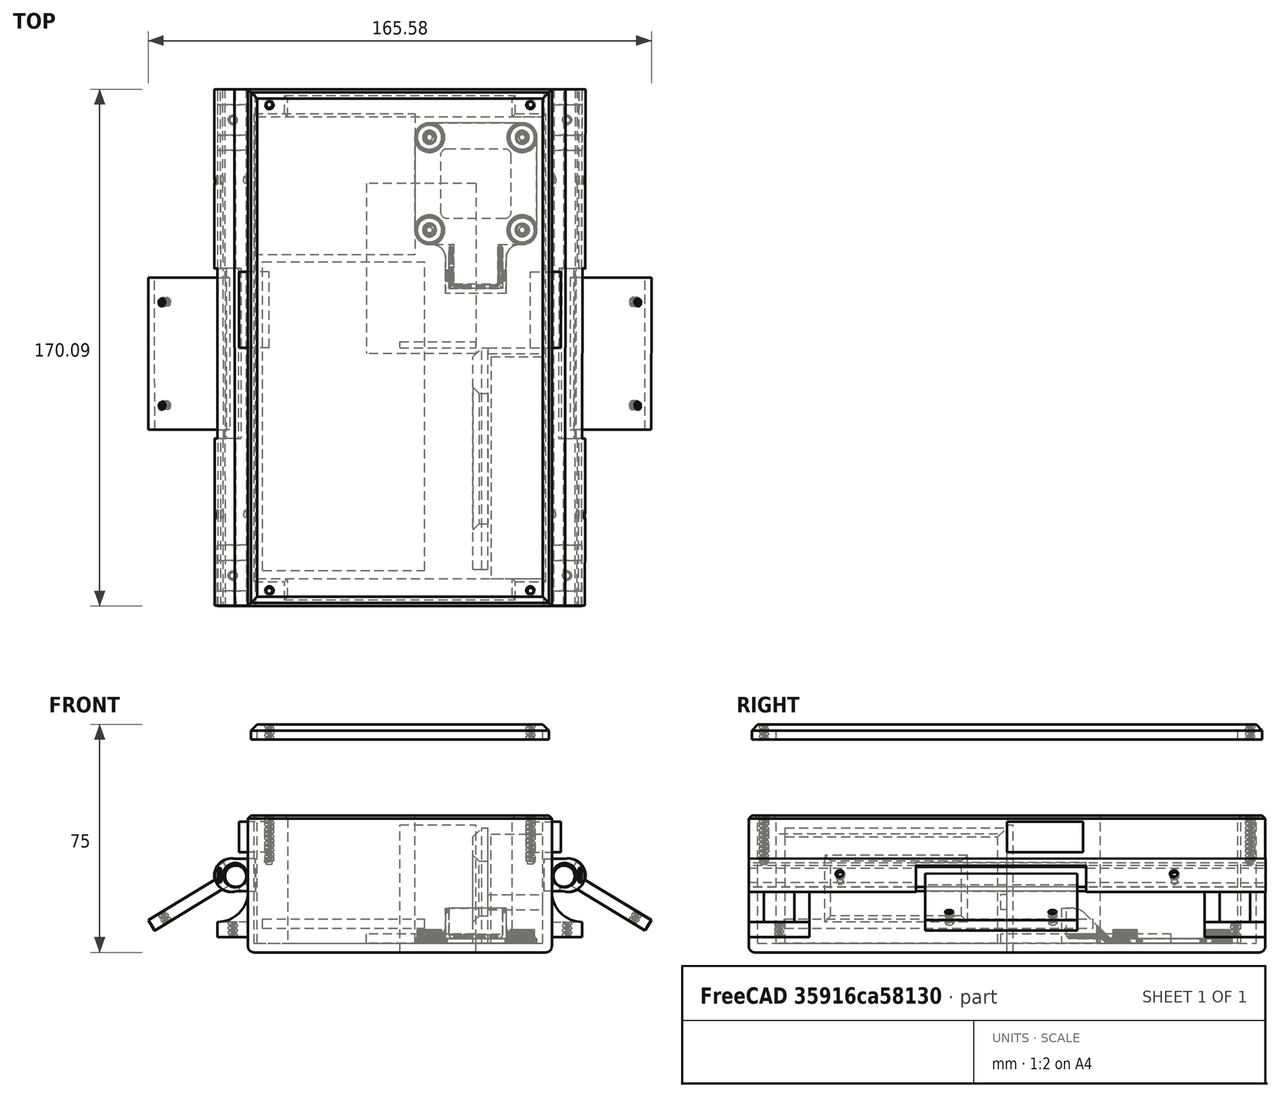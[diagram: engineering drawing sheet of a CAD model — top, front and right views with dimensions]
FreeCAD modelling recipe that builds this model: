
FCSTD DOCUMENT  (FreeCAD 0.21R33694 (Git))
Label: boceto-carcasa-reducido
License: Creative Commons Attribution-NonCommercial-ShareAlike 4.0
LicenseURL: https://creativecommons.org/licenses/by-nc-sa/4.0/
objects: Part::Box×18, Part::Fuse×14, Part::Cut×13, Part::Mirroring×10, Part::Feature×9, Part::Chamfer×5, Sketcher::SketchObject×3, Part::Cylinder×3, Part::Extrusion×3, Part::Fillet×2, Mesh::Feature×1, Part::MultiFuse×1, Part::Compound×1, App::LinkGroup×1, PartDesign::FeatureBase×1, PartDesign::Body×1
note: 84 computed .brp shape members not serialized (recipe doc carries the construction recipe); baked Part::Feature solids carry a one-line shape summary decoded from their .brp

FEATURE [Sketcher::SketchObject] Sketch  label="case-taladros"
  FullyConstrained = true
  MapMode = 5
  Support = -> [XY_Plane]
  sketch-geometry (4):
    g0: LineSegment StartX=-50 StartY=85 StartZ=0 EndX=50 EndY=85 EndZ=0
    g1: LineSegment StartX=50 StartY=85 StartZ=0 EndX=50 EndY=-85 EndZ=0
    g2: LineSegment StartX=50 StartY=-85 StartZ=0 EndX=-50 EndY=-85 EndZ=0
    g3: LineSegment StartX=-50 StartY=-85 StartZ=0 EndX=-50 EndY=85 EndZ=0
  constraints (10):
    c: Coincident(g0,g1)
    c: Coincident(g1,g2)
    c: Coincident(g2,g3)
    c: Coincident(g3,g0)
    c: Horizontal(g2)
    c: Vertical(g1)
    c: Symmetric(g0,g0,g-2)
    c: Symmetric(g2,g0,g-1)
    c: DistanceY(g3,g3) = 170
    c: DistanceX(g0,g0) = 100
FEATURE [Part::Box] Box001  label="vaciado"
  AttacherType = Attacher::AttachEngine3D
  Height = 42
  Length = 94
  Placement = pos=(-47,-76,3) rot=(0,0,1;0rad)
  Width = 152
FEATURE [Mesh::Feature] Arduino_Bumper_0005  label="Arduino-uno-case"
  Placement = pos=(-19,-40,5) rot=(0,0,1;-1.5708rad)
FEATURE [Sketcher::SketchObject] Sketch008  label="tapa-taladros"
  FullyConstrained = true
  MapMode = 5
  sketch-geometry (4):
    g0: LineSegment StartX=-49 StartY=84 StartZ=0 EndX=49 EndY=84 EndZ=0
    g1: LineSegment StartX=49 StartY=84 StartZ=0 EndX=49 EndY=-84 EndZ=0
    g2: LineSegment StartX=49 StartY=-84 StartZ=0 EndX=-49 EndY=-84 EndZ=0
    g3: LineSegment StartX=-49 StartY=-84 StartZ=0 EndX=-49 EndY=84 EndZ=0
  constraints (10):
    c: Coincident(g0,g1)
    c: Coincident(g1,g2)
    c: Coincident(g2,g3)
    c: Coincident(g3,g0)
    c: Horizontal(g2)
    c: Vertical(g1)
    c: Symmetric(g0,g0,g-2)
    c: Symmetric(g2,g0,g-1)
    c: DistanceY(g3,g3) = 168
    c: DistanceX(g0,g0) = 98
FEATURE [Part::Box] Box010  label="restriccion-lipo"
  AttacherType = Attacher::AttachEngine3D
  Height = 38
  Length = 5
  Placement = pos=(17,-75,5) rot=(0,0,1;0rad)
  Width = 73
FEATURE [Part::Box] Box011  label="restriccion-lipo001"
  AttacherType = Attacher::AttachEngine3D
  Height = 18
  Length = 7
  Placement = pos=(16,-60,14) rot=(0,0,1;0rad)
  Width = 43
FEATURE [Part::Cut] Cut028
  Base = -> Box010
  Refine = true
  Tool = -> Box011
FEATURE [Part::Chamfer] Chamfer002
  Base = -> Cut028
  Edges = 2 edges r=3: [Edge2,Edge4]
FEATURE [Part::Chamfer] Chamfer003
  Base = -> Chamfer002
  Edges = 4 edges r=2: [Edge5,Edge6,Edge7,Edge8]
FEATURE [Part::Box] Box012  label="Cube004"
  AttacherType = Attacher::AttachEngine3D
  Height = 5
  Length = 20
  Placement = pos=(20,-4,16) rot=(0,0,1;0rad)
  Width = 2
FEATURE [Part::Fuse] Fusion001032  label="rejillas-lipo"
  Base = -> Chamfer003
  Placement = pos=(7,2,-2) rot=(0,0,1;0rad)
  Refine = true
  Tool = -> Box012
FEATURE [Part::Box] Box013  label="PDB-space"
  AttacherType = Attacher::AttachEngine3D
  Height = 3
  Length = 36
  Placement = pos=(25,54,3) rot=(0,0,1;3.14159rad)
  Width = 56
FEATURE [Part::Feature] Compound001  label="pcb-support"
  Placement = pos=(25,54,3) rot=(0,0,1;3.14159rad)
  shape: bbox 40 x 56.1 x 12 mm, 27565 faces, 3 solids (baked)
FEATURE [Part::Box] Box014  label="free-space"
  AttacherType = Attacher::AttachEngine3D
  Height = 42
  Length = 46.3
  Placement = pos=(-48,77,3) rot=(0,0,-1;1.5708rad)
  Width = 53
FEATURE [Part::Box] Box015  label="Cubo002"
  AttacherType = Attacher::AttachEngine3D
  Height = 4
  Length = 50
  Placement = pos=(-25,22,-7.5) rot=(0,0,1;0rad)
  Width = 30
FEATURE [Part::Box] Box016  label="cubo-corte"
  AttacherType = Attacher::AttachEngine3D
  Height = 20
  Length = 56
  Placement = pos=(-145,75,-20) rot=(0,0,1;0rad)
  Width = 16
FEATURE [Part::Cylinder] Cylinder007  label="Cilindro-movil"
  Angle = 360
  AttacherType = Attacher::AttachEngine3D
  FirstAngle = 0
  Height = 170
  Placement = pos=(-200,92,-6) rot=(0,1,0;1.5708rad)
  Radius = 3.5
  SecondAngle = 0
FEATURE [Part::Feature] Fusion001034  label="Rosca macho012"
  Placement = pos=(-17,27,-10) rot=(0,0,1;0rad)
  shape: bbox 3.919 x 4.387 x 44 mm, 35 faces (baked)
FEATURE [Part::Feature] Fusion001035  label="Rosca macho013"
  Placement = pos=(17,27,-10) rot=(0,0,1;0rad)
  shape: bbox 3.919 x 4.387 x 44 mm, 35 faces (baked)
FEATURE [Part::MultiFuse] Fusion001036
  Refine = true
  Shapes = -> [Fusion001034,Fusion001035]
FEATURE [Part::Cut] Cut030  label="Soporte_eje001"
  Base = -> Box015
  Placement = pos=(-117,38,0) rot=(0,0,1;0rad)
  Refine = true
  Tool = -> Fusion001036
FEATURE [Part::Feature] Fusion001037  label="Rosca macho014"
  Placement = pos=(-170,93.75,-8.78) rot=(0.819304,0.219813,-0.52955;0.936369rad)
  shape: bbox 4.221 x 33 x 32.52 mm, 35 faces (baked)
FEATURE [Part::Feature] Fusion001038  label="Rosca macho015"
  Placement = pos=(-60,93.75,-8.78) rot=(0.819304,0.219813,-0.52955;0.936369rad)
  shape: bbox 4.221 x 33 x 32.52 mm, 35 faces (baked)
FEATURE [Part::Fuse] Fusion001033  label="roscas002"
  Base = -> Fusion001037
  Refine = true
  Tool = -> Fusion001038
FEATURE [Part::Fuse] Fusion001039  label="cilindro-movil001"
  Base = -> Cut030
  Refine = true
  Tool = -> Cylinder007
FEATURE [Sketcher::SketchObject] Sketch009
  FullyConstrained = false
  MapMode = 5
  Placement = pos=(0,0,0) rot=(0.57735,0.57735,0.57735;2.0944rad)
  Support = -> [YZ_Plane004]
  sketch-geometry (9):
    g0: ArcOfCircle CenterX=0 CenterY=0 CenterZ=0 NormalX=0 NormalY=0 NormalZ=1 AngleXU=0 Radius=5.5 StartAngle=6.08579 EndAngle=9.70025
    g1: Circle CenterX=0 CenterY=-1.19343 CenterZ=0 NormalX=0 NormalY=0 NormalZ=1 AngleXU=0 Radius=4
    g2: LineSegment StartX=-2.36 StartY=4.37566 StartZ=0 EndX=2.36 EndY=4.37566 EndZ=0
    g3: LineSegment StartX=2.36 StartY=4.37566 StartZ=0 EndX=2.36 EndY=3.44566 EndZ=0
    g4: LineSegment StartX=2.36 StartY=3.44566 StartZ=0 EndX=-2.36 EndY=3.44566 EndZ=0
    g5: LineSegment StartX=-2.36 StartY=3.44566 StartZ=0 EndX=-2.36 EndY=4.37566 EndZ=0
    g6: LineSegment StartX=-5.29263 StartY=-1.49602 StartZ=0 EndX=-5.29263 EndY=-8 EndZ=0
    g7: LineSegment StartX=-5.29263 StartY=-8 StartZ=0 EndX=5.39319 EndY=-8 EndZ=0
    g8: LineSegment StartX=5.39319 StartY=-8 StartZ=0 EndX=5.39319 EndY=-1.07864 EndZ=0
  constraints (21):
    c: Coincident(g0,g-1)
    c: Coincident(g2,g3)
    c: Coincident(g3,g4)
    c: Coincident(g4,g5)
    c: Coincident(g5,g2)
    c: Horizontal(g4)
    c: Vertical(g3)
    c: Vertical(g5)
    c: Symmetric(g2,g2,g-2)
    c: PointOnObject(g1,g-2)
    c: Radius(g0) = 5.5
    c: Radius(g1) = 4
    c: DistanceY(g5,g5) = 0.93
    c: DistanceX(g2,g2) = 4.72
    c: Coincident(g6,g7)
    c: Coincident(g7,g8)
    c: Horizontal(g7)
    c: Vertical(g6)
    c: Vertical(g8)
    c: Coincident(g0,g8)
    c: Coincident(g6,g0)
FEATURE [Part::Extrusion] Extrude003  label="cilindro-fijo001"
  Base = -> Sketch009
  Dir = (1,-1e-16,1e-16)
  DirMode = 2
  FaceMakerClass = Part::FaceMakerBullseye
  LengthFwd = 170
  LengthRev = 0
  Placement = pos=(-200,91,-5) rot=(1,0,0;1.02974rad)
  Solid = true
  Symmetric = false
FEATURE [Part::Cut] Cut029
  Base = -> Extrude003
  Refine = true
  Tool = -> Fusion001033
FEATURE [Part::Cut] Cut031  label="fijacion-brazo"
  Base = -> Cut029
  Refine = true
  Tool = -> Box016
FEATURE [Part::Compound] Compound  label="brazo-mejorados"
  Links = -> [Cut031,Fusion001039]
  Placement = pos=(136,115,-16.54) rot=(0.259987,0.259987,0.929954;1.64236rad)
FEATURE [Part::Mirroring] Part__Mirroring014  label="brazo-mejorados (Mirror #13)"
  Base = (0,0,0)
  Normal = (1,0,0)
  Source = -> Compound
FEATURE [Part::Extrusion] Extrude  label="carcasa-extruida"
  Base = -> Sketch
  Dir = (0,0,1)
  DirMode = 2
  FaceMakerClass = Part::FaceMakerBullseye
  LengthFwd = 45
  LengthRev = 0
  Solid = true
  Symmetric = false
FEATURE [Part::Box] Box019  label="vaciado001"
  AttacherType = Attacher::AttachEngine3D
  Height = 42
  Length = 74
  Placement = pos=(-37,-82,3) rot=(0,0,1;0rad)
  Width = 164
FEATURE [Part::Cut] Cut
  Base = -> Extrude
  Refine = true
  Tool = -> Box001
FEATURE [Part::Cut] Cut034
  Base = -> Cut
  Refine = true
  Tool = -> Box019
FEATURE [Part::Chamfer] Chamfer
  Base = -> Cut034
  Edges = 4 edges r=1: [Edge4,Edge7,Edge10,Edge12]
FEATURE [Part::Chamfer] Chamfer005
  Base = -> Chamfer
  Edges = 12 edges r=1: [Edge20,Edge21,Edge22,Edge23,Edge24,Edge25,Edge26,Edge27,Edge28,Edge29,Edge30,Edge31]
FEATURE [Part::Fillet] Fillet  label="carcasa-chaflanada"
  Base = -> Chamfer005
  Edges = 4 edges r=2: [Edge75,Edge77,Edge79,Edge80]
FEATURE [Part::Fuse] Fusion001040  label="brazos-v2"
  Base = -> Compound
  Placement = pos=(0,0,-1) rot=(0,0,1;0rad)
  Refine = true
  Tool = -> Part__Mirroring014
FEATURE [Part::Cylinder] Cylinder006  label="rellenados001"
  Angle = 360
  AttacherType = Attacher::AttachEngine3D
  FirstAngle = 0
  Height = 15
  Placement = pos=(-43,80,30) rot=(0,0,1;0rad)
  Radius = 1.5
  SecondAngle = 0
FEATURE [Part::Extrusion] Extrude004
  Base = -> Sketch008
  Dir = (0,0,1)
  DirMode = 2
  FaceMakerClass = Part::FaceMakerBullseye
  LengthFwd = 5
  LengthRev = 0
  Placement = pos=(0,0,45) rot=(0,0,1;0rad)
  Solid = true
  Symmetric = false
FEATURE [Part::Chamfer] Chamfer006  label="tapa"
  Base = -> Extrude004
  Edges = 4 edges r=2: [Edge4,Edge7,Edge10,Edge12]
FEATURE [Part::Box] Box  label="Cube"
  AttacherType = Attacher::AttachEngine3D
  Height = 5
  Length = 10
  Width = 20
FEATURE [Part::Box] Box020  label="Cube001"
  AttacherType = Attacher::AttachEngine3D
  Height = 50
  Length = 5
  Placement = pos=(-5,0,0) rot=(0,0,1;0rad)
  Width = 20
FEATURE [Part::Box] Box002  label="Cube002"
  AttacherType = Attacher::AttachEngine3D
  Height = 50
  Length = 5
  Placement = pos=(-5,0,0) rot=(0,0,1;0rad)
  Width = 20
FEATURE [Part::Box] Box003  label="Cube003"
  AttacherType = Attacher::AttachEngine3D
  Height = 20
  Length = 10
  Placement = pos=(0,5,5) rot=(0,0,1;0rad)
  Width = 10
FEATURE [Part::Cylinder] Cylinder
  Angle = 360
  AttacherType = Attacher::AttachEngine3D
  FirstAngle = 0
  Height = 6
  Placement = pos=(5,10,0) rot=(0,0,1;0rad)
  Radius = 0.5
  SecondAngle = 0
FEATURE [Part::Fuse] Fusion001047
  Base = -> Box
  Refine = true
  Tool = -> Box020
FEATURE [Part::Fillet] Fillet001
  Base = -> Fusion001047
  Edges = 1 edges r=9.99: [Edge5]
FEATURE [Part::Cut] Cut035
  Base = -> Fillet001
  Refine = true
  Tool = -> Box002
FEATURE [Part::Cut] Cut001
  Base = -> Cut035
  Refine = true
  Tool = -> Box003
FEATURE [Part::Cut] Cut002  label="acople"
  Base = -> Cut001
  Refine = true
  Tool = -> Cylinder
FEATURE [Part::Feature] Fusion001001  label="Rosca macho002"
  Placement = pos=(5,10,-9) rot=(0,0,1;0rad)
  shape: bbox 3.919 x 4.387 x 44 mm, 35 faces (baked)
FEATURE [Part::Cut] Cut003  label="acople-roscado"
  Base = -> Cut002
  Placement = pos=(50,-85,5) rot=(0,0,1;0rad)
  Refine = true
  Tool = -> Fusion001001
FEATURE [Part::Mirroring] Part__Mirroring021  label="acople-roscado (Mirror #7)"
  Base = (0,0,0)
  Normal = (1,0,0)
  Source = -> Cut003
FEATURE [Part::Fuse] Fusion001048
  Base = -> Cut003
  Refine = true
  Tool = -> Part__Mirroring021
FEATURE [Part::Mirroring] Part__Mirroring022  label="Fusion001048 (Mirror #8)"
  Base = (0,0,0)
  Normal = (0,1,0)
  Source = -> Fusion001048
FEATURE [Part::Fuse] Fusion001049  label="acoples-flotador"
  Base = -> Fusion001048
  Refine = true
  Tool = -> Part__Mirroring022
FEATURE [Part::Feature] Compound002  label="simple-rosca"
  Placement = pos=(43,-80,30) rot=(0,0,1;0rad)
  shape: bbox 3.919 x 4.387 x 44 mm, 65 faces (baked)
FEATURE [Part::Mirroring] Part__Mirroring  label="rellenados001 (Mirror #8)"
  Base = (0,0,0)
  Normal = (0,1,0)
  Source = -> Cylinder006
FEATURE [Part::Fuse] Fusion
  Base = -> Cylinder006
  Refine = true
  Tool = -> Part__Mirroring
FEATURE [Part::Mirroring] Part__Mirroring018  label="Fusion (Mirror #9)"
  Base = (0,0,0)
  Normal = (1,0,0)
  Source = -> Fusion
FEATURE [Part::Fuse] Fusion001044  label="posicion-roscas"
  Base = -> Fusion
  Refine = true
  Tool = -> Part__Mirroring018
FEATURE [Part::Mirroring] Part__Mirroring023  label="simple-rosca (Mirror #7)"
  Base = (0,0,0)
  Normal = (1,0,0)
  Source = -> Compound002
FEATURE [Part::Fuse] Fusion001050
  Base = -> Compound002
  Refine = true
  Tool = -> Part__Mirroring023
FEATURE [Part::Mirroring] Part__Mirroring024  label="roscas-4"
  Base = (0,0,0)
  Normal = (0,1,0)
  Source = -> Fusion001050
FEATURE [Part::Fuse] Fusion001051  label="roscas-carcasa"
  Base = -> Fusion001050
  Refine = true
  Tool = -> Part__Mirroring024
FEATURE [Part::Feature] Compound003  label="simple-rosca001"
  Placement = pos=(43,-80,30) rot=(0,0,1;0rad)
  shape: bbox 3.919 x 4.387 x 44 mm, 65 faces (baked)
FEATURE [Part::Mirroring] Part__Mirroring025  label="simple-rosca (Mirror #7)001"
  Base = (0,0,0)
  Normal = (1,0,0)
  Source = -> Compound003
FEATURE [Part::Fuse] Fusion001052
  Base = -> Compound003
  Refine = true
  Tool = -> Part__Mirroring025
FEATURE [Part::Mirroring] Part__Mirroring026  label="roscas-005"
  Base = (0,0,0)
  Normal = (0,1,0)
  Source = -> Fusion001052
FEATURE [Part::Fuse] Fusion001053  label="roscas-tapa"
  Base = -> Fusion001052
  Refine = true
  Tool = -> Part__Mirroring026
FEATURE [Part::Cut] Cut036  label="carcasa-roscada-15mm"
  Base = -> Fillet
  Refine = true
  Tool = -> Fusion001051
FEATURE [Part::Cut] Cut037  label="tapa-roscada-5mm"
  Base = -> Chamfer006
  Placement = pos=(0,0,25) rot=(0,0,1;0rad)
  Refine = true
  Tool = -> Fusion001053
FEATURE [Part::Box] Box021  label="agujeros-new"
  AttacherType = Attacher::AttachEngine3D
  Height = 10
  Length = 10
  Placement = pos=(43,0,33) rot=(0,0,1;0rad)
  Width = 25
FEATURE [Part::Mirroring] Part__Mirroring027  label="agujeros-new (Mirror #11)"
  Base = (0,0,0)
  Normal = (1,0,0)
  Source = -> Box021
FEATURE [Part::Fuse] Fusion001054  label="agujeros-rectangulares"
  Base = -> Box021
  Refine = true
  Tool = -> Part__Mirroring027
FEATURE [Part::Feature] Compound004  label="arduino-mega-case-solid"
  Placement = pos=(-62,80,3) rot=(0,0,-1;1.5708rad)
  shape: bbox 57.6 x 106.6 x 5.8 mm, 182 faces (baked)
FEATURE [Part::Box] Box022  label="lipo-space"
  AttacherType = Attacher::AttachEngine3D
  Height = 36
  Length = 73
  Placement = pos=(30,-3,3) rot=(0,0,-1;1.5708rad)
  Width = 17
FEATURE [Part::Box] Box023  label="arduino-mega-space"
  AttacherType = Attacher::AttachEngine3D
  Height = 3
  Length = 53.3
  Placement = pos=(-45.15,-73.26,8) rot=(0,0,1;0rad)
  Width = 101.52
FEATURE [Part::Box] Box024  label="receptor-space"
  AttacherType = Attacher::AttachEngine3D
  Height = 42
  Length = 25
  Placement = pos=(-47,68,3) rot=(0,0,-1;1.5708rad)
  Width = 2
FEATURE [App::LinkGroup] LinkGroup  label="componentes-shell"
  ElementList = -> [Compound001,Box013,Box014,Fusion001032,Arduino_Bumper_0005,Compound004,Box022,Box023,Box024]
  LinkMode = 0
FEATURE [PartDesign::FeatureBase] BaseFeature
  BaseFeature = -> Box024
FEATURE [PartDesign::Body] Body  label="carcasa-boceto"
  BaseFeature = -> Box024
  Group = -> [BaseFeature,Sketch]
  Origin = -> Origin
  Tip = -> BaseFeature
FEATURE [Part::Box] Box025  label="vaciado002"
  AttacherType = Attacher::AttachEngine3D
  Height = 3
  Length = 94
  Placement = pos=(-47,-76,70) rot=(0,0,1;0rad)
  Width = 152
FEATURE [Part::Cut] Cut038  label="tapa-roscada-5mm001"
  Base = -> Cut037
  Refine = true
  Tool = -> Box025
